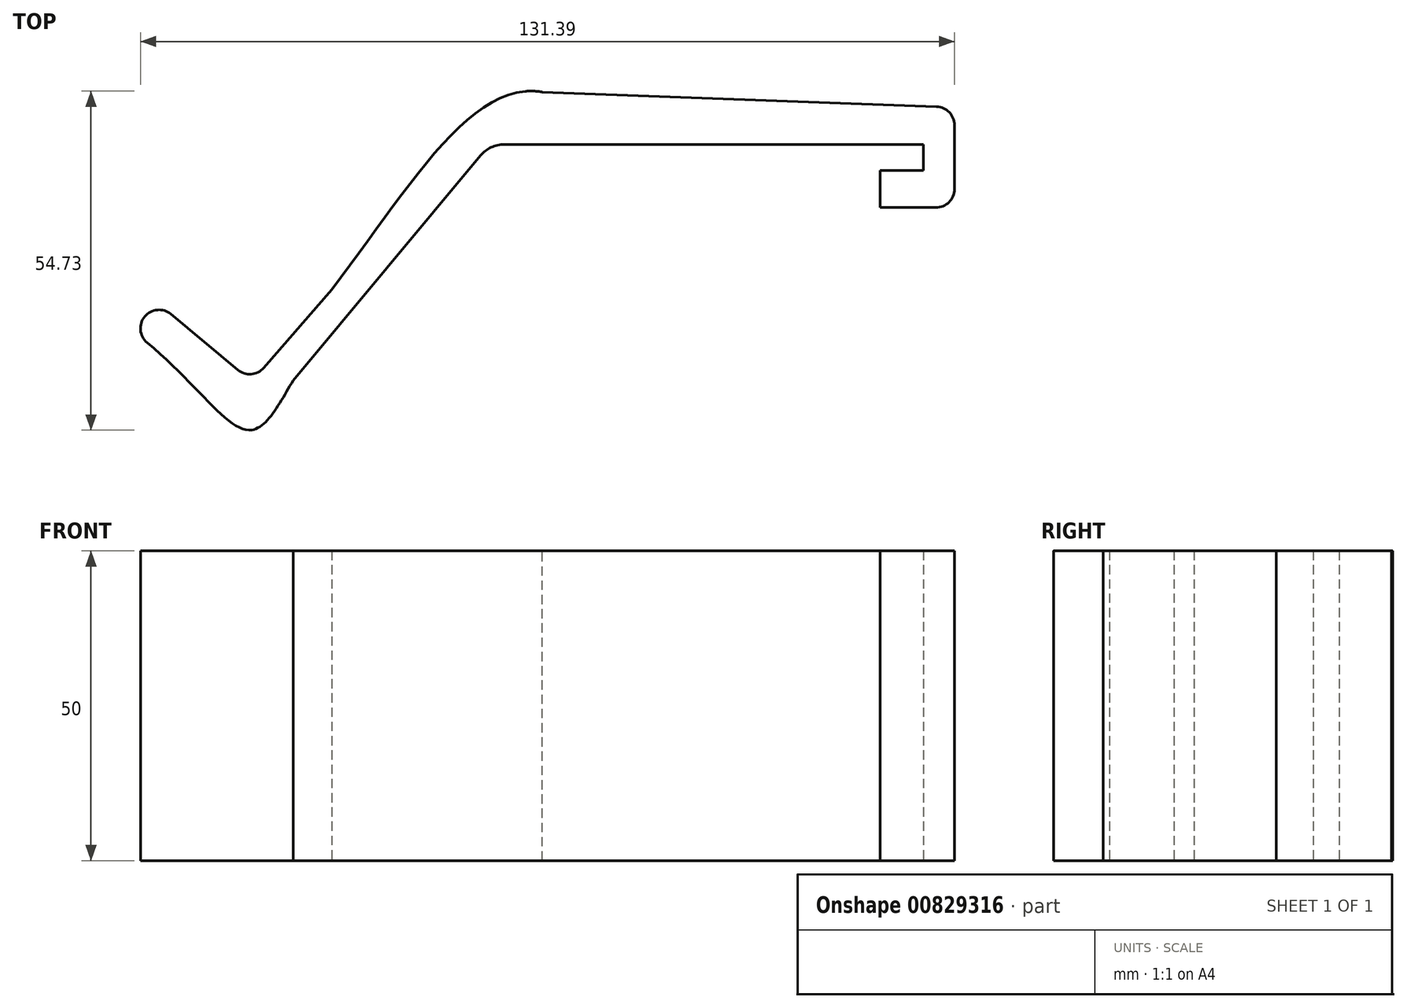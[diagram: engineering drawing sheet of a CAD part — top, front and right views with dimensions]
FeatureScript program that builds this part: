
annotation { "Feature Type Name" : "Feature", "Feature Type Description" : "" }
export const myFeature = defineFeature(function(context is Context, id is Id, definition is map)
    precondition{}
    {
        {
            var Q0;
            Q0=qCreatedBy(makeId("Top.planeOp"),FACE);
            var sketch = newSketch(context, id + "F0", { "sketchPlane" : qUnion([Q0])});
            skLineSegment(sketch, "E0", {"start": v(-51.18, 21.2) * mm, "end": v(22.82, 21.2) * mm});
            skLineSegment(sketch, "E1", {"start": v(22.82, 21.2) * mm, "end": v(22.82, 17.2) * mm});
            skLineSegment(sketch, "E2", {"start": v(22.82, 17.2) * mm, "end": v(-51.18, 17.2) * mm});
            skLineSegment(sketch, "E3", {"start": v(-51.18, 17.2) * mm, "end": v(-51.18, 21.2) * mm});
            skLineSegment(sketch, "E4", {"start": v(22.82, 17.2) * mm, "end": v(22.82, 13.2) * mm});
            skLineSegment(sketch, "E5", {"start": v(22.82, 13.2) * mm, "end": v(12.82, 13.2) * mm});
            skLineSegment(sketch, "E6", {"start": v(12.82, 13.2) * mm, "end": v(12.82, 15.7) * mm});
            skLineSegment(sketch, "E7", {"start": v(12.82, 15.7) * mm, "end": v(15.32, 15.7) * mm});
            skLineSegment(sketch, "E8", {"start": v(15.32, 15.7) * mm, "end": v(19.12, 15.7) * mm});
            skLineSegment(sketch, "E9", {"start": v(19.12, 15.7) * mm, "end": v(19.12, 17.2) * mm});
            skLineSegment(sketch, "E10", {"start": v(-90.08, -16.16) * mm, "end": v(-51.18, 21.2) * mm});
            skLineSegment(sketch, "E11", {"start": v(-51.18, 17.2) * mm, "end": v(-90.08, -20.16) * mm});
            skLineSegment(sketch, "E12", {"start": v(-90.08, -16.16) * mm, "end": v(-90.08, -20.16) * mm});
            skLineSegment(sketch, "E13", {"start": v(-90.08, -20.16) * mm, "end": v(-97, -12.95) * mm});
            skLineSegment(sketch, "E14", {"start": v(-97, -12.95) * mm, "end": v(-90.08, -16.16) * mm});
            skLineSegment(sketch, "E15", {"start": v(-90.08, -16.16) * mm, "end": v(-97, -8.95) * mm});
            skLineSegment(sketch, "E16", {"start": v(-97, -8.95) * mm, "end": v(-97, -12.95) * mm});
            skLineSegment(sketch, "E17", {"start": v(-97, -12.95) * mm, "end": v(-103.96, -5.7) * mm});
            skLineSegment(sketch, "E18", {"start": v(-103.96, -5.7) * mm, "end": v(-97, -8.95) * mm});
            skLineSegment(sketch, "E19", {"start": v(-97, -8.95) * mm, "end": v(-103.96, 0) * mm});
            skLineSegment(sketch, "E20", {"start": v(-103.96, 0) * mm, "end": v(-103.96, -5.7) * mm});
            skCircle(sketch, "E21", {"center": v(-90.08, -20.16) * mm, "radius": 4.18 * mm});
            skLineSegment(sketch, "E22", {"start": v(-93.55, -22.5) * mm, "end": v(-103.96, -5.7) * mm});
            skPoint(sketch, "E22.startSnap0", {"position": v(-93.55, -12.56) * mm});
            skLineSegment(sketch, "E23", {"start": v(-85.9, -20.16) * mm, "end": v(-51.18, 17.2) * mm});
            skSolve(sketch);
        }
        {
            var Q0;
            {var subQ0=sQuery(id+"F0.wireOp",EDGE,"E4");Q0=makeQuery(id+"F0.imprint","IMPRINT",FACE,{"disambiguationData":[TD([[makeQuery(id+"F0.imprint","IMPRINT",EDGE,{"derivedFrom":subQ0}),-1.0]])]});}
            var sketch = newSketch(context, id + "F1", { "sketchPlane" : qUnion([Q0])});
            skLineSegment(sketch, "E24.bottom", {"start": v(-63.66, 58.82) * mm, "end": v(5.43, 58.82) * mm});
            skLineSegment(sketch, "E24.top", {"start": v(-62.23, 52.82) * mm, "end": v(5.43, 52.82) * mm});
            skLineSegment(sketch, "E24.left", {"start": v(-64.57, 58.82) * mm, "end": v(-64.57, 52.82) * mm});
            skLineSegment(sketch, "E24.right", {"start": v(5.43, 58.82) * mm, "end": v(5.43, 52.82) * mm});
            skLineSegment(sketch, "E25", {"start": v(-66.07, 51.02) * mm, "end": v(-102.98, 6.73) * mm});
            skLineSegment(sketch, "E26", {"start": v(-102.98, 6.73) * mm, "end": v(-119.88, 20.81) * mm});
            skLineSegment(sketch, "E27", {"start": v(-120.27, 25.04) * mm, "end": v(-120.27, 25.04) * mm});
            skLineSegment(sketch, "E28", {"start": v(-116.04, 25.42) * mm, "end": v(-105.24, 16.42) * mm});
            skLineSegment(sketch, "E29", {"start": v(-101.06, 16.76) * mm, "end": v(-65.17, 58.13) * mm});
            skLineSegment(sketch, "E30", {"start": v(5.43, 52.82) * mm, "end": v(5.43, 48.62) * mm});
            skLineSegment(sketch, "E31", {"start": v(5.43, 48.62) * mm, "end": v(-1.57, 48.62) * mm});
            skLineSegment(sketch, "E32", {"start": v(-1.57, 48.62) * mm, "end": v(-1.57, 42.62) * mm});
            skLineSegment(sketch, "E33", {"start": v(-1.57, 42.62) * mm, "end": v(7.43, 42.62) * mm});
            skLineSegment(sketch, "E34", {"start": v(10.43, 45.62) * mm, "end": v(10.43, 55.93) * mm});
            skPoint(sketch, "E35.2.internal.snap0", {"position": v(-112.59, 14.73) * mm});
            skFitSpline(sketch, "E35", {"points": [v(-119.9, 20.83) * mm, v(-102.98, 6.73) * mm, v(-96.31, 14.73) * mm], "startDerivative": vector(42.9, -35.75) * mm, "endDerivative": vector(15.02, 25.16) * mm});
            skPoint(sketch, "E36.visualSharp", {"position": v(-64.57, 58.82) * mm});
            skArc(sketch, "E36.filletArc", {"start": v(-63.66, 58.82) * mm, "mid": v(-64.49, 58.64) * mm, "end": v(-65.17, 58.13) * mm});
            skPoint(sketch, "E37.visualSharp", {"position": v(-118.35, 27.34) * mm});
            skArc(sketch, "E37.filletArc", {"start": v(-116.04, 25.42) * mm, "mid": v(-118.24, 26.1) * mm, "end": v(-120.27, 25.04) * mm});
            skPoint(sketch, "E38.visualSharp", {"position": v(-122.19, 22.73) * mm});
            skArc(sketch, "E38.filletArc", {"start": v(-120.27, 25.04) * mm, "mid": v(-120.95, 22.85) * mm, "end": v(-119.88, 20.81) * mm});
            skPoint(sketch, "E39.visualSharp", {"position": v(-102.98, 14.54) * mm});
            skArc(sketch, "E39.filletArc", {"start": v(-105.24, 16.42) * mm, "mid": v(-103.08, 15.74) * mm, "end": v(-101.06, 16.76) * mm});
            skPoint(sketch, "E40.visualSharp", {"position": v(-64.57, 52.82) * mm});
            skArc(sketch, "E40.filletArc", {"start": v(-62.23, 52.82) * mm, "mid": v(-64.35, 52.35) * mm, "end": v(-66.07, 51.02) * mm});
            skFitSpline(sketch, "E41", {"points": [v(-101.06, 16.76) * mm, v(-50.38, 58.82) * mm], "startDerivative": vector(61.15, 59.59) * mm, "endDerivative": vector(53.52, -37.13) * mm});
            skLineSegment(sketch, "E42", {"start": v(-58.86, 61.39) * mm, "end": v(7.54, 58.93) * mm});
            skArc(sketch, "E43.filletArc", {"start": v(10.43, 55.93) * mm, "mid": v(9.59, 58.01) * mm, "end": v(7.54, 58.93) * mm});
            skPoint(sketch, "E44.visualSharp", {"position": v(10.43, 42.62) * mm});
            skArc(sketch, "E44.filletArc", {"start": v(7.43, 42.62) * mm, "mid": v(9.55, 43.5) * mm, "end": v(10.43, 45.62) * mm});
            skSolve(sketch);
        }
        {
            var Q0;
            {var subQ0=sQuery(id+"F0.wireOp",EDGE,"E4");Q0=makeQuery(id+"F1.imprint","IMPRINT",FACE,{"disambiguationData":[TD([[makeQuery(id+"F1.imprint","IMPRINT",EDGE,{"derivedFrom":makeQuery(id+"F0.imprint","IMPRINT",EDGE,{"derivedFrom":subQ0})}),-1.0]])]});}
            var Q1;
            Q1=makeQuery(id+"F1.imprint","IMPRINT",FACE,{"disambiguationData":[TD([[makeQuery(id+"F1.imprint","IMPRINT",EDGE,{"derivedFrom":sQuery(id+"F1.wireOp",EDGE,"E24.top")}),1.0]])]});
            var Q2;
            {var subQ0=sQuery(id+"F1.wireOp",EDGE,"E41");var subQ1=sQuery(id+"F1.wireOp",EDGE,"E29");var subQ3=makeQuery(id+"F1.imprint","INTERSECT",VERTEX,{"derivedFrom":[subQ1,subQ0]});Q2=makeQuery(id+"F1.imprint","IMPRINT",FACE,{"disambiguationData":[TD([[makeQuery(id+"F1.imprint","IMPRINT",EDGE,{"disambiguationData":[TD([[subQ3,1.0]])],"derivedFrom":subQ1}),-1.0]])]});}
            var Q3;
            {var subQ0=sQuery(id+"F1.wireOp",EDGE,"E36.filletArc");var subQ3=makeQuery(id+"F1.imprint","IMPRINT",VERTEX,{"derivedFrom":subQ0});Q3=makeQuery(id+"F1.imprint","IMPRINT",FACE,{"disambiguationData":[TD([[makeQuery(id+"F1.imprint","IMPRINT",EDGE,{"disambiguationData":[TD([[subQ3,1.0]])],"derivedFrom":subQ0}),-1.0]])]});}
            var Q4;
            {var subQ6=sQuery(id+"F1.wireOp",EDGE,"E24.right");Q4=makeQuery(id+"F1.imprint","IMPRINT",FACE,{"disambiguationData":[TD([[makeQuery(id+"F1.imprint","IMPRINT",EDGE,{"derivedFrom":subQ6}),1.0]])]});}
            var Q5;
            {var subQ0=sQuery(id+"F1.wireOp",EDGE,"E42");var subQ1=sQuery(id+"F1.wireOp",EDGE,"E41");var subQ2=makeQuery(id+"F1.imprint","INTERSECT",VERTEX,{"disambiguationData":[OD(0.0)],"derivedFrom":[subQ1,subQ0]});Q5=makeQuery(id+"F1.imprint","IMPRINT",FACE,{"disambiguationData":[TD([[makeQuery(id+"F1.imprint","IMPRINT",EDGE,{"disambiguationData":[TD([[subQ2,-1.0]])],"derivedFrom":subQ1}),-1.0]])]});}
            var Q6;
            {var subQ0=sQuery(id+"F1.wireOp",EDGE,"E35");var subQ1=sQuery(id+"F1.wireOp",EDGE,"E25");var subQ3=makeQuery(id+"F1.imprint","INTERSECT",VERTEX,{"derivedFrom":[subQ1,subQ0]});Q6=makeQuery(id+"F1.imprint","IMPRINT",FACE,{"disambiguationData":[TD([[makeQuery(id+"F1.imprint","IMPRINT",EDGE,{"disambiguationData":[TD([[subQ3,-1.0]])],"derivedFrom":subQ1}),1.0]])]});}
            var Q7;
            {var subQ0=sQuery(id+"F1.wireOp",EDGE,"E26");Q7=makeQuery(id+"F1.imprint","IMPRINT",FACE,{"disambiguationData":[TD([[makeQuery(id+"F1.imprint","IMPRINT",EDGE,{"derivedFrom":subQ0}),1.0]])]});}
            extrude(context, id + "F2", {"entities" : qUnion([Q0, Q1, Q2, Q3, Q4, Q5, Q6, Q7]), "depth" : 50 * mm, "offsetDistance" : 25 * mm});
        }
        {
            var Q0;
            Q0=makeQuery(id+"F2.opExtrude","SWEPT_BODY",BODY,{"disambiguationData":[OSD([sQuery(id+"F0.wireOp",EDGE,"E2"),sQuery(id+"F0.wireOp",EDGE,"E4"),sQuery(id+"F0.wireOp",EDGE,"E5"),sQuery(id+"F0.wireOp",EDGE,"E6"),sQuery(id+"F0.wireOp",EDGE,"E7"),sQuery(id+"F0.wireOp",EDGE,"E8"),sQuery(id+"F0.wireOp",EDGE,"E9")])]});
            deleteBodies(context, id + "F3", {"entities" : qUnion([Q0])});
        }
    });
